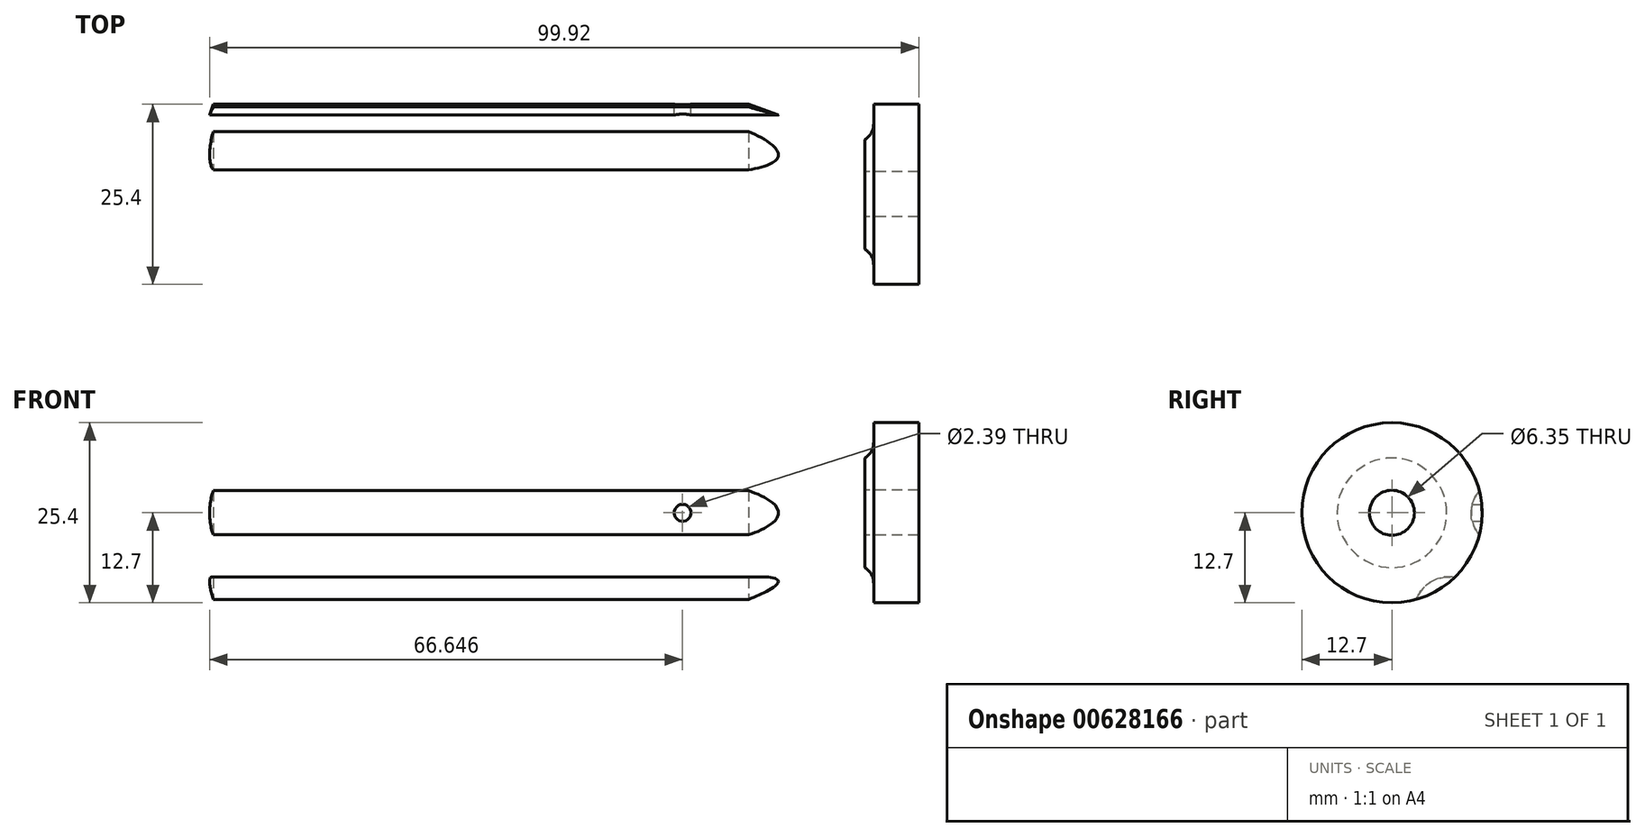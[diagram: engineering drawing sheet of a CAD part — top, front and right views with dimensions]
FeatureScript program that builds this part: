
annotation { "Feature Type Name" : "Feature", "Feature Type Description" : "" }
export const myFeature = defineFeature(function(context is Context, id is Id, definition is map)
    precondition{}
    {
        {
            var Q0;
            Q0=qCreatedBy(makeId("Front.planeOp"),FACE);
            var sketch = newSketch(context, id + "F0", { "sketchPlane" : qUnion([Q0])});
            skLineSegment(sketch, "E0", {"start": v(-40.64, 0) * mm, "end": v(-40.64, 3.18) * mm});
            skLineSegment(sketch, "E1", {"start": v(-40.64, 3.18) * mm, "end": v(0, 3.18) * mm});
            skLineSegment(sketch, "E2", {"start": v(0, 3.18) * mm, "end": v(0, 12.7) * mm});
            skLineSegment(sketch, "E3", {"start": v(0, 12.7) * mm, "end": v(-6.35, 12.7) * mm});
            skLineSegment(sketch, "E4", {"start": v(-6.35, 12.7) * mm, "end": v(-6.35, 9.92) * mm});
            skLineSegment(sketch, "E5", {"start": v(-9.76, 7.54) * mm, "end": v(-23.95, 12.7) * mm});
            skLineSegment(sketch, "E6", {"start": v(-23.95, 12.7) * mm, "end": v(-99.42, 12.7) * mm});
            skLineSegment(sketch, "E7", {"start": v(-101.6, 0) * mm, "end": v(-40.64, 0) * mm});
            skPoint(sketch, "E8.visualSharp", {"position": v(-6.35, 6.3) * mm});
            skArc(sketch, "E8.filletArc", {"start": v(-9.76, 7.54) * mm, "mid": v(-7.43, 7.84) * mm, "end": v(-6.35, 9.92) * mm});
            skArc(sketch, "E9", {"start": v(-99.42, 12.7) * mm, "mid": v(-101.05, 6.44) * mm, "end": v(-101.6, 0) * mm});
            skSolve(sketch);
        }
        {
            var Q0;
            Q0 = qSketchRegion(id + "F0", true);
            var Q1;
            Q1=sQuery(id+"F0.wireOp",EDGE,"E7");
            revolve(context, id + "F1", {"entities" : qUnion([Q0]), "axis" : qUnion([Q1]), "revolveType" : RevolveType.FULL});
        }
        {
            var Q0;
            Q0=qCreatedBy(makeId("Right.planeOp"),FACE);
            var sketch = newSketch(context, id + "F2", { "sketchPlane" : qUnion([Q0])});
            skCircle(sketch, "E10", {"center": v(0, 0) * mm, "radius": 16 * mm});
            skCircle(sketch, "E11", {"center": v(-16, 0) * mm, "radius": 4.83 * mm});
            skCircle(sketch, "E12.1.0", {"center": v(-8, -13.86) * mm, "radius": 4.83 * mm});
            skCircle(sketch, "E12.2.0", {"center": v(8, -13.86) * mm, "radius": 4.83 * mm});
            skCircle(sketch, "E12.3.0", {"center": v(16, 0) * mm, "radius": 4.83 * mm});
            skCircle(sketch, "E12.4.0", {"center": v(8, 13.86) * mm, "radius": 4.83 * mm});
            skCircle(sketch, "E12.5.0", {"center": v(-8, 13.86) * mm, "radius": 4.83 * mm});
            skSolve(sketch);
        }
        {
            var Q0;
            {var subQ0=sQuery(id+"F2.wireOp",EDGE,"E12.5.0");var subQ1=sQuery(id+"F2.wireOp",EDGE,"E10");var subQ2=makeQuery(id+"F2.imprint","INTERSECT",VERTEX,{"disambiguationData":[OD(0.0)],"derivedFrom":[subQ1,subQ0]});Q0=makeQuery(id+"F2.imprint","IMPRINT",FACE,{"disambiguationData":[TD([[makeQuery(id+"F2.imprint","IMPRINT",EDGE,{"disambiguationData":[TD([[subQ2,-1.0]])],"derivedFrom":subQ1}),1.0]])]});}
            var Q1;
            {var subQ0=sQuery(id+"F2.wireOp",EDGE,"E12.4.0");var subQ1=sQuery(id+"F2.wireOp",EDGE,"E10");var subQ2=makeQuery(id+"F2.imprint","INTERSECT",VERTEX,{"disambiguationData":[OD(0.0)],"derivedFrom":[subQ1,subQ0]});Q1=makeQuery(id+"F2.imprint","IMPRINT",FACE,{"disambiguationData":[TD([[makeQuery(id+"F2.imprint","IMPRINT",EDGE,{"disambiguationData":[TD([[subQ2,-1.0]])],"derivedFrom":subQ1}),1.0]])]});}
            var Q2;
            {var subQ0=sQuery(id+"F2.wireOp",EDGE,"E12.3.0");var subQ1=sQuery(id+"F2.wireOp",EDGE,"E10");var subQ2=makeQuery(id+"F2.imprint","INTERSECT",VERTEX,{"disambiguationData":[OD(0.0)],"derivedFrom":[subQ1,subQ0]});Q2=makeQuery(id+"F2.imprint","IMPRINT",FACE,{"disambiguationData":[TD([[makeQuery(id+"F2.imprint","IMPRINT",EDGE,{"disambiguationData":[TD([[subQ2,1.0]])],"derivedFrom":subQ1}),1.0]])]});}
            var Q3;
            {var subQ0=sQuery(id+"F2.wireOp",EDGE,"E12.2.0");var subQ1=sQuery(id+"F2.wireOp",EDGE,"E10");var subQ2=makeQuery(id+"F2.imprint","INTERSECT",VERTEX,{"disambiguationData":[OD(0.0)],"derivedFrom":[subQ1,subQ0]});Q3=makeQuery(id+"F2.imprint","IMPRINT",FACE,{"disambiguationData":[TD([[makeQuery(id+"F2.imprint","IMPRINT",EDGE,{"disambiguationData":[TD([[subQ2,-1.0]])],"derivedFrom":subQ1}),1.0]])]});}
            var Q4;
            {var subQ0=sQuery(id+"F2.wireOp",EDGE,"E12.1.0");var subQ1=sQuery(id+"F2.wireOp",EDGE,"E10");var subQ2=makeQuery(id+"F2.imprint","INTERSECT",VERTEX,{"disambiguationData":[OD(0.0)],"derivedFrom":[subQ1,subQ0]});Q4=makeQuery(id+"F2.imprint","IMPRINT",FACE,{"disambiguationData":[TD([[makeQuery(id+"F2.imprint","IMPRINT",EDGE,{"disambiguationData":[TD([[subQ2,-1.0]])],"derivedFrom":subQ1}),1.0]])]});}
            var Q5;
            {var subQ0=sQuery(id+"F2.wireOp",EDGE,"E11");var subQ1=sQuery(id+"F2.wireOp",EDGE,"E10");var subQ2=makeQuery(id+"F2.imprint","INTERSECT",VERTEX,{"disambiguationData":[OD(0.0)],"derivedFrom":[subQ1,subQ0]});Q5=makeQuery(id+"F2.imprint","IMPRINT",FACE,{"disambiguationData":[TD([[makeQuery(id+"F2.imprint","IMPRINT",EDGE,{"disambiguationData":[TD([[subQ2,-1.0]])],"derivedFrom":subQ1}),1.0]])]});}
            extrude(context, id + "F3", {"entities" : qUnion([Q0, Q1, Q2, Q3, Q4, Q5]), "operationType" : NewBodyOperationType.REMOVE, "endBound" : BoundingType.THROUGH_ALL, "oppositeDirection" : true, "depth" : 25.4 * mm, "offsetDistance" : 25.4 * mm, "hasSecondDirection" : true, "secondDirectionOppositeDirection" : true, "secondDirectionDepth" : 7.62 * mm});
        }
        {
            var Q0;
            Q0=qCreatedBy(makeId("Front.planeOp"),FACE);
            var sketch = newSketch(context, id + "F4", { "sketchPlane" : qUnion([Q0])});
            skCircle(sketch, "E13", {"center": v(-33.27, 0) * mm, "radius": 1.2 * mm});
            skSolve(sketch);
        }
        {
            var Q0;
            Q0 = qSketchRegion(id + "F4", true);
            extrude(context, id + "F5", {"entities" : qUnion([Q0]), "operationType" : NewBodyOperationType.REMOVE, "endBound" : BoundingType.SYMMETRIC, "depth" : 25.4 * mm, "offsetDistance" : 25.4 * mm});
        }
    });
